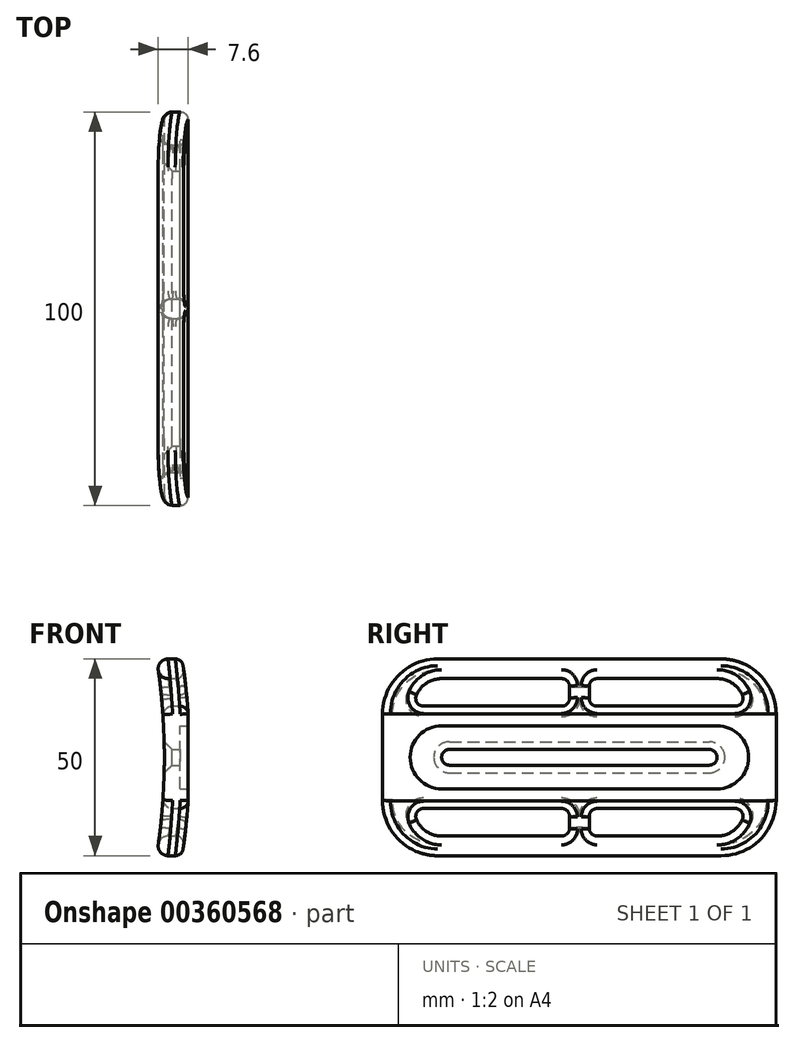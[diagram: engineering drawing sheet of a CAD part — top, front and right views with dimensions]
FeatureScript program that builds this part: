
annotation { "Feature Type Name" : "Feature", "Feature Type Description" : "" }
export const myFeature = defineFeature(function(context is Context, id is Id, definition is map)
    precondition{}
    {
        {
            var Q0;
            Q0=qCreatedBy(makeId("Front.planeOp"),FACE);
            var sketch = newSketch(context, id + "F0", { "sketchPlane" : qUnion([Q0])});
            skLineSegment(sketch, "E0.top", {"start": v(0, 25) * mm, "end": v(-8, 25) * mm});
            skLineSegment(sketch, "E0.left", {"start": v(0, 0) * mm, "end": v(0, 25) * mm});
            skLineSegment(sketch, "E0.right", {"start": v(-8, 0) * mm, "end": v(-8, 25) * mm});
            skLineSegment(sketch, "E1.top", {"start": v(0, -25) * mm, "end": v(-8, -25) * mm});
            skLineSegment(sketch, "E1.left", {"start": v(0, 0) * mm, "end": v(0, -25) * mm});
            skLineSegment(sketch, "E1.right", {"start": v(-8, 0) * mm, "end": v(-8, -25) * mm});
            skLineSegment(sketch, "E2.bottom", {"start": v(0, 8) * mm, "end": v(-2, 8) * mm});
            skLineSegment(sketch, "E2.top", {"start": v(0, -8) * mm, "end": v(-2, -8) * mm});
            skLineSegment(sketch, "E2.left", {"start": v(0, 8) * mm, "end": v(0, -8) * mm});
            skLineSegment(sketch, "E2.right", {"start": v(-2, 8) * mm, "end": v(-2, -8) * mm});
            skPoint(sketch, "E3.third.point", {"position": v(-196.82, -27.04) * mm});
            skArc(sketch, "E4", {"start": v(-8, -25) * mm, "mid": v(-6.03, 0) * mm, "end": v(-8, 25) * mm});
            skPoint(sketch, "E4.third.point", {"position": v(-14.66, -51.81) * mm});
            skArc(sketch, "E5.0", {"start": v(-1.52, -25) * mm, "mid": v(-0.61, -18.03) * mm, "end": v(0, -11.02) * mm});
            skArc(sketch, "E6.trimOffspring", {"start": v(0, 11.02) * mm, "mid": v(-0.61, 18.03) * mm, "end": v(-1.52, 25) * mm});
            skSolve(sketch);
        }
        {
            var Q0;
            Q0=makeQuery(id+"F0.imprint","IMPRINT",FACE,{"disambiguationData":[TD([[makeQuery(id+"F0.imprint","IMPRINT",EDGE,{"derivedFrom":sQuery(id+"F0.wireOp",EDGE,"E2.bottom")}),-1.0]])]});
            extrude(context, id + "F1", {"entities" : qUnion([Q0]), "depth" : 50 * mm, "hasSecondDirection" : true, "secondDirectionOppositeDirection" : true, "secondDirectionDepth" : 50 * mm});
        }
        {
            var Q0;
            Q0=makeQuery(id+"F1.opExtrude","CAP_EDGE",EDGE,{"disambiguationData":[OSD([sQuery(id+"F0.wireOp",EDGE,"E0.top")])],"isStart":false});
            var Q1;
            Q1=makeQuery(id+"F1.opExtrude","CAP_EDGE",EDGE,{"disambiguationData":[OSD([sQuery(id+"F0.wireOp",EDGE,"E0.top")])],"isStart":true});
            var Q2;
            Q2=makeQuery(id+"F1.opExtrude","CAP_EDGE",EDGE,{"disambiguationData":[OSD([sQuery(id+"F0.wireOp",EDGE,"E1.top")])],"isStart":false});
            var Q3;
            Q3=makeQuery(id+"F1.opExtrude","CAP_EDGE",EDGE,{"disambiguationData":[OSD([sQuery(id+"F0.wireOp",EDGE,"E1.top")])],"isStart":true});
            fillet(context, id + "F2", {"entities" : qUnion([Q0, Q1, Q2, Q3]), "radius" : 14 * mm, "tangentPropagation" : true, "allowEdgeOverflow" : false});
        }
        {
            var Q0;
            Q0=qCreatedBy(makeId("Right.planeOp"),FACE);
            var sketch = newSketch(context, id + "F3", { "sketchPlane" : qUnion([Q0])});
            skLineSegment(sketch, "E7.bottom", {"start": v(-35, 20) * mm, "end": v(-2.5, 20) * mm});
            skLineSegment(sketch, "E7.top", {"start": v(-35, 13) * mm, "end": v(-2.5, 13) * mm});
            skLineSegment(sketch, "E7.right", {"start": v(-2.5, 20) * mm, "end": v(-2.5, 13) * mm});
            skLineSegment(sketch, "E8.bottom", {"start": v(-2.5, -20) * mm, "end": v(-35, -20) * mm});
            skLineSegment(sketch, "E8.top", {"start": v(-2.5, -13) * mm, "end": v(-35, -13) * mm});
            skLineSegment(sketch, "E8.left", {"start": v(-2.5, -20) * mm, "end": v(-2.5, -13) * mm});
            skLineSegment(sketch, "E9", {"start": v(0, 0) * mm, "end": v(0, 52.93) * mm, "construction": true});
            skLineSegment(sketch, "E10", {"start": v(0, 52.93) * mm, "end": v(-1.44, 52.93) * mm, "construction": true});
            skLineSegment(sketch, "E11.MirrorCS", {"start": v(35, 20) * mm, "end": v(2.5, 20) * mm});
            skLineSegment(sketch, "E12.MirrorCS", {"start": v(2.5, 20) * mm, "end": v(2.5, 13) * mm});
            skLineSegment(sketch, "E13.MirrorCS", {"start": v(35, 13) * mm, "end": v(2.5, 13) * mm});
            skLineSegment(sketch, "E14.MirrorCS", {"start": v(2.5, -20) * mm, "end": v(35, -20) * mm});
            skLineSegment(sketch, "E15.MirrorCS", {"start": v(2.5, -13) * mm, "end": v(35, -13) * mm});
            skLineSegment(sketch, "E16.MirrorCS", {"start": v(2.5, -20) * mm, "end": v(2.5, -13) * mm});
            skLineSegment(sketch, "E17", {"start": v(-35, 13) * mm, "end": v(-42, 13) * mm});
            skLineSegment(sketch, "E18", {"start": v(42, 13) * mm, "end": v(35, 13) * mm});
            skLineSegment(sketch, "E19", {"start": v(35, -13) * mm, "end": v(42, -13) * mm});
            skLineSegment(sketch, "E20", {"start": v(-35, -13) * mm, "end": v(-42, -13) * mm});
            skArc(sketch, "E21", {"start": v(42, 13) * mm, "mid": v(39.95, 17.95) * mm, "end": v(35, 20) * mm});
            skArc(sketch, "E22", {"start": v(-35, 20) * mm, "mid": v(-39.95, 17.95) * mm, "end": v(-42, 13) * mm});
            skArc(sketch, "E23", {"start": v(-42, -13) * mm, "mid": v(-39.95, -17.95) * mm, "end": v(-35, -20) * mm});
            skArc(sketch, "E24", {"start": v(35, -20) * mm, "mid": v(39.95, -17.95) * mm, "end": v(42, -13) * mm});
            skPoint(sketch, "E25.MirrorCS.start.orphan", {"position": v(35, 20) * mm});
            skSolve(sketch);
        }
        {
            var Q0;
            Q0=makeQuery(id+"F3.imprint","IMPRINT",FACE,{"disambiguationData":[TD([[makeQuery(id+"F3.imprint","IMPRINT",EDGE,{"derivedFrom":sQuery(id+"F3.wireOp",EDGE,"E7.bottom")}),-1.0]])]});
            var Q1;
            Q1=makeQuery(id+"F3.imprint","IMPRINT",FACE,{"disambiguationData":[TD([[makeQuery(id+"F3.imprint","IMPRINT",EDGE,{"derivedFrom":sQuery(id+"F3.wireOp",EDGE,"aYIwaKne-w7pD-jzg0-wIrR-frMYWOzJamIR.bottom")}),1.0]])]});
            var Q2;
            Q2=makeQuery(id+"F3.imprint","IMPRINT",FACE,{"disambiguationData":[TD([[makeQuery(id+"F3.imprint","IMPRINT",EDGE,{"derivedFrom":sQuery(id+"F3.wireOp",EDGE,"dbu9yMfO-LKLj-5adb-XFTp-mxRKxUa9Af3I.bottom")}),1.0]])]});
            var Q3;
            Q3=makeQuery(id+"F3.imprint","IMPRINT",FACE,{"disambiguationData":[TD([[makeQuery(id+"F3.imprint","IMPRINT",EDGE,{"derivedFrom":sQuery(id+"F3.wireOp",EDGE,"E8.bottom")}),-1.0]])]});
            var Q4;
            Q4=makeQuery(id+"F3.imprint","IMPRINT",FACE,{"disambiguationData":[TD([[makeQuery(id+"F3.imprint","IMPRINT",EDGE,{"derivedFrom":sQuery(id+"F3.wireOp",EDGE,"E11.MirrorCS")}),1.0]])]});
            var Q5;
            Q5=makeQuery(id+"F3.imprint","IMPRINT",FACE,{"disambiguationData":[TD([[makeQuery(id+"F3.imprint","IMPRINT",EDGE,{"derivedFrom":sQuery(id+"F3.wireOp",EDGE,"a9c6f0e5-25e9-4c5a-a24e-b3d4f0bb53d11.MirrorCS")}),-1.0]])]});
            var Q6;
            Q6=makeQuery(id+"F3.imprint","IMPRINT",FACE,{"disambiguationData":[TD([[makeQuery(id+"F3.imprint","IMPRINT",EDGE,{"derivedFrom":sQuery(id+"F3.wireOp",EDGE,"a9c6f0e5-25e9-4c5a-a24e-b3d4f0bb53d10.MirrorCS")}),-1.0]])]});
            var Q7;
            Q7=makeQuery(id+"F3.imprint","IMPRINT",FACE,{"disambiguationData":[TD([[makeQuery(id+"F3.imprint","IMPRINT",EDGE,{"derivedFrom":sQuery(id+"F3.wireOp",EDGE,"E14.MirrorCS")}),1.0]])]});
            var Q8;
            Q8=makeQuery(id+"F3.imprint","IMPRINT",FACE,{"disambiguationData":[TD([[makeQuery(id+"F3.imprint","IMPRINT",EDGE,{"derivedFrom":sQuery(id+"F3.wireOp",EDGE,"E7.left")}),-1.0]])]});
            var Q9;
            Q9=makeQuery(id+"F3.imprint","IMPRINT",FACE,{"disambiguationData":[TD([[makeQuery(id+"F3.imprint","IMPRINT",EDGE,{"derivedFrom":sQuery(id+"F3.wireOp",EDGE,"E25.MirrorCS")}),1.0]])]});
            var Q10;
            Q10=makeQuery(id+"F3.imprint","IMPRINT",FACE,{"disambiguationData":[TD([[makeQuery(id+"F3.imprint","IMPRINT",EDGE,{"derivedFrom":sQuery(id+"F3.wireOp",EDGE,"6a068f12-1f97-4c15-ac1c-3f1accc7e67e0.MirrorCS")}),-1.0]])]});
            var Q11;
            Q11=makeQuery(id+"F3.imprint","IMPRINT",FACE,{"disambiguationData":[TD([[makeQuery(id+"F3.imprint","IMPRINT",EDGE,{"derivedFrom":sQuery(id+"F3.wireOp",EDGE,"E8.right")}),1.0]])]});
            extrude(context, id + "F4", {"entities" : qUnion([Q0, Q1, Q2, Q3, Q4, Q5, Q6, Q7, Q8, Q9, Q10, Q11]), "operationType" : NewBodyOperationType.REMOVE, "oppositeDirection" : true, "depth" : 25 * mm});
        }
        {
            var Q0;
            Q0=qCreatedBy(makeId("Right.planeOp"),FACE);
            var sketch = newSketch(context, id + "F5", { "sketchPlane" : qUnion([Q0])});
            skLineSegment(sketch, "E26.bottom", {"start": v(-35, 2) * mm, "end": v(35, 2) * mm});
            skLineSegment(sketch, "E26.top", {"start": v(-35, -2) * mm, "end": v(35, -2) * mm});
            skLineSegment(sketch, "E26.left", {"start": v(-35, 2) * mm, "end": v(-35, -2) * mm});
            skLineSegment(sketch, "E26.right", {"start": v(35, 2) * mm, "end": v(35, -2) * mm});
            skSolve(sketch);
        }
        {
            var Q0;
            Q0=makeQuery(id+"F5.imprint","IMPRINT",FACE,{"disambiguationData":[TD([[makeQuery(id+"F5.imprint","IMPRINT",EDGE,{"derivedFrom":sQuery(id+"F5.wireOp",EDGE,"E26.bottom")}),-1.0]])]});
            extrude(context, id + "F6", {"entities" : qUnion([Q0]), "operationType" : NewBodyOperationType.REMOVE, "oppositeDirection" : true, "depth" : 25 * mm});
        }
        {
            var Q0;
            Q0=qCreatedBy(makeId("Right.planeOp"),FACE);
            var sketch = newSketch(context, id + "F7", { "sketchPlane" : qUnion([Q0])});
            skLineSegment(sketch, "E27", {"start": v(0, 0) * mm, "end": v(-35, 0) * mm, "construction": true});
            skArc(sketch, "E28", {"start": v(-35, 8) * mm, "mid": v(-43, 0) * mm, "end": v(-35, -8) * mm});
            skLineSegment(sketch, "E29", {"start": v(0, 0) * mm, "end": v(35, 0) * mm, "construction": true});
            skArc(sketch, "E30", {"start": v(35, -8) * mm, "mid": v(43, 0) * mm, "end": v(35, 8) * mm});
            skLineSegment(sketch, "E31", {"start": v(-35, 0) * mm, "end": v(-35, -8) * mm, "construction": true});
            skLineSegment(sketch, "E32", {"start": v(-35, -8) * mm, "end": v(-50, -8) * mm});
            skLineSegment(sketch, "E33", {"start": v(-35, 0) * mm, "end": v(-35, 8) * mm, "construction": true});
            skLineSegment(sketch, "E34", {"start": v(-35, 8) * mm, "end": v(-50, 8) * mm});
            skLineSegment(sketch, "E35", {"start": v(-50, 8) * mm, "end": v(-50, -8) * mm});
            skLineSegment(sketch, "E36", {"start": v(35, 0) * mm, "end": v(35, 8) * mm, "construction": true});
            skLineSegment(sketch, "E37", {"start": v(35, 8) * mm, "end": v(50, 8) * mm});
            skLineSegment(sketch, "E38", {"start": v(35, 0) * mm, "end": v(35, -8) * mm, "construction": true});
            skLineSegment(sketch, "E39", {"start": v(35, -8) * mm, "end": v(50, -8) * mm});
            skLineSegment(sketch, "E40", {"start": v(50, -8) * mm, "end": v(50, 8) * mm});
            skPoint(sketch, "E41.orphan", {"position": v(51.81, 8) * mm});
            skSolve(sketch);
        }
        {
            var Q0;
            Q0=qSketchRegion(id+"F7",true);
            extrude(context, id + "F8", {"entities" : qUnion([Q0]), "operationType" : NewBodyOperationType.ADD, "oppositeDirection" : true, "depth" : 3 * mm});
        }
        {
            var Q0;
            Q0=makeQuery(id+"F4.boolean.opBoolean","COPY",EDGE,{"derivedFrom":makeQuery(id+"F4.opExtrude","SWEPT_EDGE",EDGE,{"disambiguationData":[OSD([sQuery(id+"F3.wireOp",EDGE,"E7.bottom"),sQuery(id+"F3.wireOp",EDGE,"E7.right")])]})});
            var Q1;
            Q1=makeQuery(id+"F4.boolean.opBoolean","COPY",EDGE,{"derivedFrom":makeQuery(id+"F4.opExtrude","SWEPT_EDGE",EDGE,{"disambiguationData":[OSD([sQuery(id+"F3.wireOp",EDGE,"E8.top"),sQuery(id+"F3.wireOp",EDGE,"E8.left")])]})});
            var Q2;
            Q2=makeQuery(id+"F4.boolean.opBoolean","COPY",EDGE,{"derivedFrom":makeQuery(id+"F4.opExtrude","SWEPT_EDGE",EDGE,{"disambiguationData":[OSD([sQuery(id+"F3.wireOp",EDGE,"E8.bottom"),sQuery(id+"F3.wireOp",EDGE,"E8.left")])]})});
            var Q3;
            Q3=makeQuery(id+"F4.boolean.opBoolean","COPY",EDGE,{"derivedFrom":makeQuery(id+"F4.opExtrude","SWEPT_EDGE",EDGE,{"disambiguationData":[OSD([sQuery(id+"F3.wireOp",EDGE,"E7.top"),sQuery(id+"F3.wireOp",EDGE,"E7.right")])]})});
            var Q4;
            Q4=makeQuery(id+"F4.boolean.opBoolean","COPY",EDGE,{"derivedFrom":makeQuery(id+"F4.opExtrude","SWEPT_EDGE",EDGE,{"disambiguationData":[OSD([sQuery(id+"F3.wireOp",EDGE,"E18"),sQuery(id+"F3.wireOp",EDGE,"E21")])]})});
            var Q5;
            Q5=makeQuery(id+"F4.boolean.opBoolean","COPY",EDGE,{"derivedFrom":makeQuery(id+"F4.opExtrude","SWEPT_EDGE",EDGE,{"disambiguationData":[OSD([sQuery(id+"F3.wireOp",EDGE,"E19"),sQuery(id+"F3.wireOp",EDGE,"E24")])]})});
            var Q6;
            Q6=makeQuery(id+"F4.boolean.opBoolean","COPY",EDGE,{"derivedFrom":makeQuery(id+"F4.opExtrude","SWEPT_EDGE",EDGE,{"disambiguationData":[OSD([sQuery(id+"F3.wireOp",EDGE,"E11.MirrorCS"),sQuery(id+"F3.wireOp",EDGE,"E12.MirrorCS")])]})});
            var Q7;
            Q7=makeQuery(id+"F4.boolean.opBoolean","COPY",EDGE,{"derivedFrom":makeQuery(id+"F4.opExtrude","SWEPT_EDGE",EDGE,{"disambiguationData":[OSD([sQuery(id+"F3.wireOp",EDGE,"E15.MirrorCS"),sQuery(id+"F3.wireOp",EDGE,"E16.MirrorCS")])]})});
            var Q8;
            Q8=makeQuery(id+"F4.boolean.opBoolean","COPY",EDGE,{"derivedFrom":makeQuery(id+"F4.opExtrude","SWEPT_EDGE",EDGE,{"disambiguationData":[OSD([sQuery(id+"F3.wireOp",EDGE,"E20"),sQuery(id+"F3.wireOp",EDGE,"E23")])]})});
            var Q9;
            Q9=makeQuery(id+"F4.boolean.opBoolean","COPY",EDGE,{"derivedFrom":makeQuery(id+"F4.opExtrude","SWEPT_EDGE",EDGE,{"disambiguationData":[OSD([sQuery(id+"F3.wireOp",EDGE,"E12.MirrorCS"),sQuery(id+"F3.wireOp",EDGE,"E13.MirrorCS")])]})});
            var Q10;
            Q10=makeQuery(id+"F4.boolean.opBoolean","COPY",EDGE,{"derivedFrom":makeQuery(id+"F4.opExtrude","SWEPT_EDGE",EDGE,{"disambiguationData":[OSD([sQuery(id+"F3.wireOp",EDGE,"E14.MirrorCS"),sQuery(id+"F3.wireOp",EDGE,"E16.MirrorCS")])]})});
            var Q11;
            Q11=makeQuery(id+"F4.boolean.opBoolean","COPY",EDGE,{"derivedFrom":makeQuery(id+"F4.opExtrude","SWEPT_EDGE",EDGE,{"disambiguationData":[OSD([sQuery(id+"F3.wireOp",EDGE,"E17"),sQuery(id+"F3.wireOp",EDGE,"E22")])]})});
            fillet(context, id + "F9", {"entities" : qUnion([Q0, Q1, Q2, Q3, Q4, Q5, Q6, Q7, Q8, Q9, Q10, Q11]), "radius" : 2 * mm, "tangentPropagation" : true, "allowEdgeOverflow" : false});
        }
        {
            var Q0;
            Q0=makeQuery(id+"F6.boolean.opBoolean","COPY",EDGE,{"derivedFrom":makeQuery(id+"F6.opExtrude","SWEPT_EDGE",EDGE,{"disambiguationData":[OSD([sQuery(id+"F5.wireOp",EDGE,"E26.top"),sQuery(id+"F5.wireOp",EDGE,"E26.right")])]})});
            var Q1;
            Q1=makeQuery(id+"F6.boolean.opBoolean","COPY",EDGE,{"derivedFrom":makeQuery(id+"F6.opExtrude","SWEPT_EDGE",EDGE,{"disambiguationData":[OSD([sQuery(id+"F5.wireOp",EDGE,"E26.top"),sQuery(id+"F5.wireOp",EDGE,"E26.left")])]})});
            var Q2;
            Q2=makeQuery(id+"F6.boolean.opBoolean","COPY",EDGE,{"derivedFrom":makeQuery(id+"F6.opExtrude","SWEPT_EDGE",EDGE,{"disambiguationData":[OSD([sQuery(id+"F5.wireOp",EDGE,"E26.bottom"),sQuery(id+"F5.wireOp",EDGE,"E26.right")])]})});
            var Q3;
            Q3=makeQuery(id+"F6.boolean.opBoolean","COPY",EDGE,{"derivedFrom":makeQuery(id+"F6.opExtrude","SWEPT_EDGE",EDGE,{"disambiguationData":[OSD([sQuery(id+"F5.wireOp",EDGE,"E26.bottom"),sQuery(id+"F5.wireOp",EDGE,"E26.left")])]})});
            fillet(context, id + "F10", {"entities" : qUnion([Q0, Q1, Q2, Q3]), "radius" : 2 * mm, "tangentPropagation" : true, "allowEdgeOverflow" : false});
        }
        {
            var Q0;
            Q0=makeQuery(id+"F6.boolean.opBoolean","INTERSECT",EDGE,{"derivedFrom":[makeQuery(id+"F1.opExtrude","SWEPT_FACE",FACE,{"disambiguationData":[OSD([sQuery(id+"F0.wireOp",EDGE,"E4")])]}),makeQuery(id+"F6.opExtrude","SWEPT_FACE",FACE,{"disambiguationData":[OSD([sQuery(id+"F5.wireOp",EDGE,"E26.bottom")])]})]});
            chamfer(context, id + "F11", {"entities" : qUnion([Q0]), "width" : 2 * mm, "tangentPropagation" : true});
        }
        {
            var Q0;
            Q0=makeQuery(id+"F4.boolean.opBoolean","INTERSECT",EDGE,{"derivedFrom":[makeQuery(id+"F1.opExtrude","SWEPT_FACE",FACE,{"disambiguationData":[OSD([sQuery(id+"F0.wireOp",EDGE,"E4")])]}),makeQuery(id+"F4.opExtrude","SWEPT_FACE",FACE,{"disambiguationData":[OSD([sQuery(id+"F3.wireOp",EDGE,"E11.MirrorCS")])]})]});
            var Q1;
            Q1=makeQuery(id+"F4.boolean.opBoolean","INTERSECT",EDGE,{"derivedFrom":[makeQuery(id+"F1.opExtrude","SWEPT_FACE",FACE,{"disambiguationData":[OSD([sQuery(id+"F0.wireOp",EDGE,"E4")])]}),makeQuery(id+"F4.opExtrude","SWEPT_FACE",FACE,{"disambiguationData":[OSD([sQuery(id+"F3.wireOp",EDGE,"E7.bottom")])]})]});
            var Q2;
            Q2=makeQuery(id+"F4.boolean.opBoolean","INTERSECT",EDGE,{"derivedFrom":[makeQuery(id+"F1.opExtrude","SWEPT_FACE",FACE,{"disambiguationData":[OSD([sQuery(id+"F0.wireOp",EDGE,"E4")])]}),makeQuery(id+"F4.opExtrude","SWEPT_FACE",FACE,{"disambiguationData":[OSD([sQuery(id+"F3.wireOp",EDGE,"E15.MirrorCS"),sQuery(id+"F3.wireOp",EDGE,"E19")])]})]});
            var Q3;
            Q3=makeQuery(id+"F4.boolean.opBoolean","INTERSECT",EDGE,{"derivedFrom":[makeQuery(id+"F1.opExtrude","SWEPT_FACE",FACE,{"disambiguationData":[OSD([sQuery(id+"F0.wireOp",EDGE,"E4")])]}),makeQuery(id+"F4.opExtrude","SWEPT_FACE",FACE,{"disambiguationData":[OSD([sQuery(id+"F3.wireOp",EDGE,"E8.top"),sQuery(id+"F3.wireOp",EDGE,"E20")])]})]});
            var Q4;
            Q4=makeQuery(id+"F1.opExtrude","SWEPT_EDGE",EDGE,{"disambiguationData":[OSD([sQuery(id+"F0.wireOp",EDGE,"E0.top"),sQuery(id+"F0.wireOp",EDGE,"E0.right"),sQuery(id+"F0.wireOp",EDGE,"E4")])]});
            fillet(context, id + "F12", {"entities" : qUnion([Q0, Q1, Q2, Q3, Q4]), "radius" : 2.5 * mm, "tangentPropagation" : true, "allowEdgeOverflow" : false});
        }
        {
            var Q0;
            Q0=makeQuery(id+"F4.boolean.opBoolean","INTERSECT",EDGE,{"derivedFrom":[makeQuery(id+"F1.opExtrude","SWEPT_FACE",FACE,{"disambiguationData":[OSD([sQuery(id+"F0.wireOp",EDGE,"E6.trimOffspring")])]}),makeQuery(id+"F4.opExtrude","SWEPT_FACE",FACE,{"disambiguationData":[OSD([sQuery(id+"F3.wireOp",EDGE,"E7.bottom")])]})]});
            var Q1;
            Q1=makeQuery(id+"F4.boolean.opBoolean","INTERSECT",EDGE,{"derivedFrom":[makeQuery(id+"F1.opExtrude","SWEPT_FACE",FACE,{"disambiguationData":[OSD([sQuery(id+"F0.wireOp",EDGE,"E6.trimOffspring")])]}),makeQuery(id+"F4.opExtrude","SWEPT_FACE",FACE,{"disambiguationData":[OSD([sQuery(id+"F3.wireOp",EDGE,"E11.MirrorCS")])]})]});
            var Q2;
            Q2=makeQuery(id+"F4.boolean.opBoolean","INTERSECT",EDGE,{"derivedFrom":[makeQuery(id+"F1.opExtrude","SWEPT_FACE",FACE,{"disambiguationData":[OSD([sQuery(id+"F0.wireOp",EDGE,"E5.0")])]}),makeQuery(id+"F4.opExtrude","SWEPT_FACE",FACE,{"disambiguationData":[OSD([sQuery(id+"F3.wireOp",EDGE,"E15.MirrorCS"),sQuery(id+"F3.wireOp",EDGE,"E19")])]})]});
            var Q3;
            Q3=makeQuery(id+"F4.boolean.opBoolean","INTERSECT",EDGE,{"derivedFrom":[makeQuery(id+"F1.opExtrude","SWEPT_FACE",FACE,{"disambiguationData":[OSD([sQuery(id+"F0.wireOp",EDGE,"E5.0")])]}),makeQuery(id+"F4.opExtrude","SWEPT_FACE",FACE,{"disambiguationData":[OSD([sQuery(id+"F3.wireOp",EDGE,"E8.top"),sQuery(id+"F3.wireOp",EDGE,"E20")])]})]});
            fillet(context, id + "F13", {"entities" : qUnion([Q0, Q1, Q2, Q3]), "radius" : 2 * mm, "tangentPropagation" : true, "allowEdgeOverflow" : false});
        }
        {
            var Q0;
            Q0=makeQuery(id+"F2.opFillet","BLEND_EDGE",EDGE,{"blendedFrom":[makeQuery(id+"F1.opExtrude","CAP_EDGE",EDGE,{"disambiguationData":[OSD([sQuery(id+"F0.wireOp",EDGE,"E0.top")])],"isStart":true}),makeQuery(id+"F1.opExtrude","SWEPT_FACE",FACE,{"disambiguationData":[OSD([sQuery(id+"F0.wireOp",EDGE,"E6.trimOffspring")])]})],"blendedInto":[makeQuery(id+"F1.opExtrude","SWEPT_FACE",FACE,{"disambiguationData":[OSD([sQuery(id+"F0.wireOp",EDGE,"E6.trimOffspring")])]})]});
            var Q1;
            Q1=makeQuery(id+"F2.opFillet","BLEND_EDGE",EDGE,{"blendedFrom":[makeQuery(id+"F1.opExtrude","CAP_EDGE",EDGE,{"disambiguationData":[OSD([sQuery(id+"F0.wireOp",EDGE,"E1.top")])],"isStart":true}),makeQuery(id+"F1.opExtrude","SWEPT_FACE",FACE,{"disambiguationData":[OSD([sQuery(id+"F0.wireOp",EDGE,"E5.0")])]})],"blendedInto":[makeQuery(id+"F1.opExtrude","SWEPT_FACE",FACE,{"disambiguationData":[OSD([sQuery(id+"F0.wireOp",EDGE,"E5.0")])]})]});
            fillet(context, id + "F14", {"entities" : qUnion([Q0, Q1]), "radius" : 2 * mm, "tangentPropagation" : true, "allowEdgeOverflow" : false});
        }
    });
